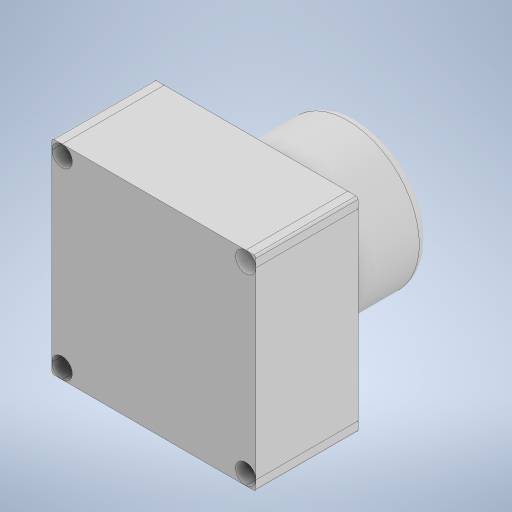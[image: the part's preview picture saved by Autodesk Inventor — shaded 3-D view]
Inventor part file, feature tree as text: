
AUTODESK INVENTOR PART (.ipt)
format: ipt  version: 2024 (Build 280153000, 153)  size: 266,240 bytes
history: native  units: in
note: dims shown in document units (in); Inventor stores cm internally (conversion verified against a paired STEP export)
features: sketch x5, fillet x5, extrude x4, thread x1
ambient origin geometry x8: Origin, YZ Plane, XZ Plane, XY Plane, X Axis, Y Axis, Z Axis, Center Point
bodies: Solid1 (feature_tree)
feature tree (15):
  extrude  "Extrusion1"  Depth=3.937in
  sketch  "Sketch2"  dims[d2=1.9685in d3=0.0in d11=3.5433in d12=3.5433in d13=1.9685in d14=0.0in d15=0.0394in d16=0.0394in]
  extrude  "Extrusion2"  Depth=0.0394in
  fillet  "Fillet1"  Radius=3.5433in
  fillet  "Fillet2"  Radius=1.9685in
  fillet  "Fillet3"  Radius=0.0394in
  fillet  "Fillet4"  Radius=0.0394in
  extrude  "Extrusion3"  Depth=0.0394in
  extrude  "Extrusion4"  Depth=2.7559in
  fillet  "Fillet5"  Radius=1.9685in
  thread  "Thread1"  [1 undecoded]
  sketch  "Sketch1"  dims[d0=3.937in d1=3.937in]
  sketch  "Sketch5"  dims[d17=0.0394in d18=0.0394in]
  sketch  "Sketch6"  dims[d20=2.7559in d21=2.7559in d22=1.9685in d23=0.0in d24=1.9685in]
  sketch  "Sketch7"  dims[d25=1.1811in d26=0.0in d27=0.1969in d28=1.1811in d29=0.0in]
note: 1 required parameter value undecoded (feature->parameter linkage not recoverable at this tier; creation-order binding heuristic only, values carry confidence <= 0.55)
